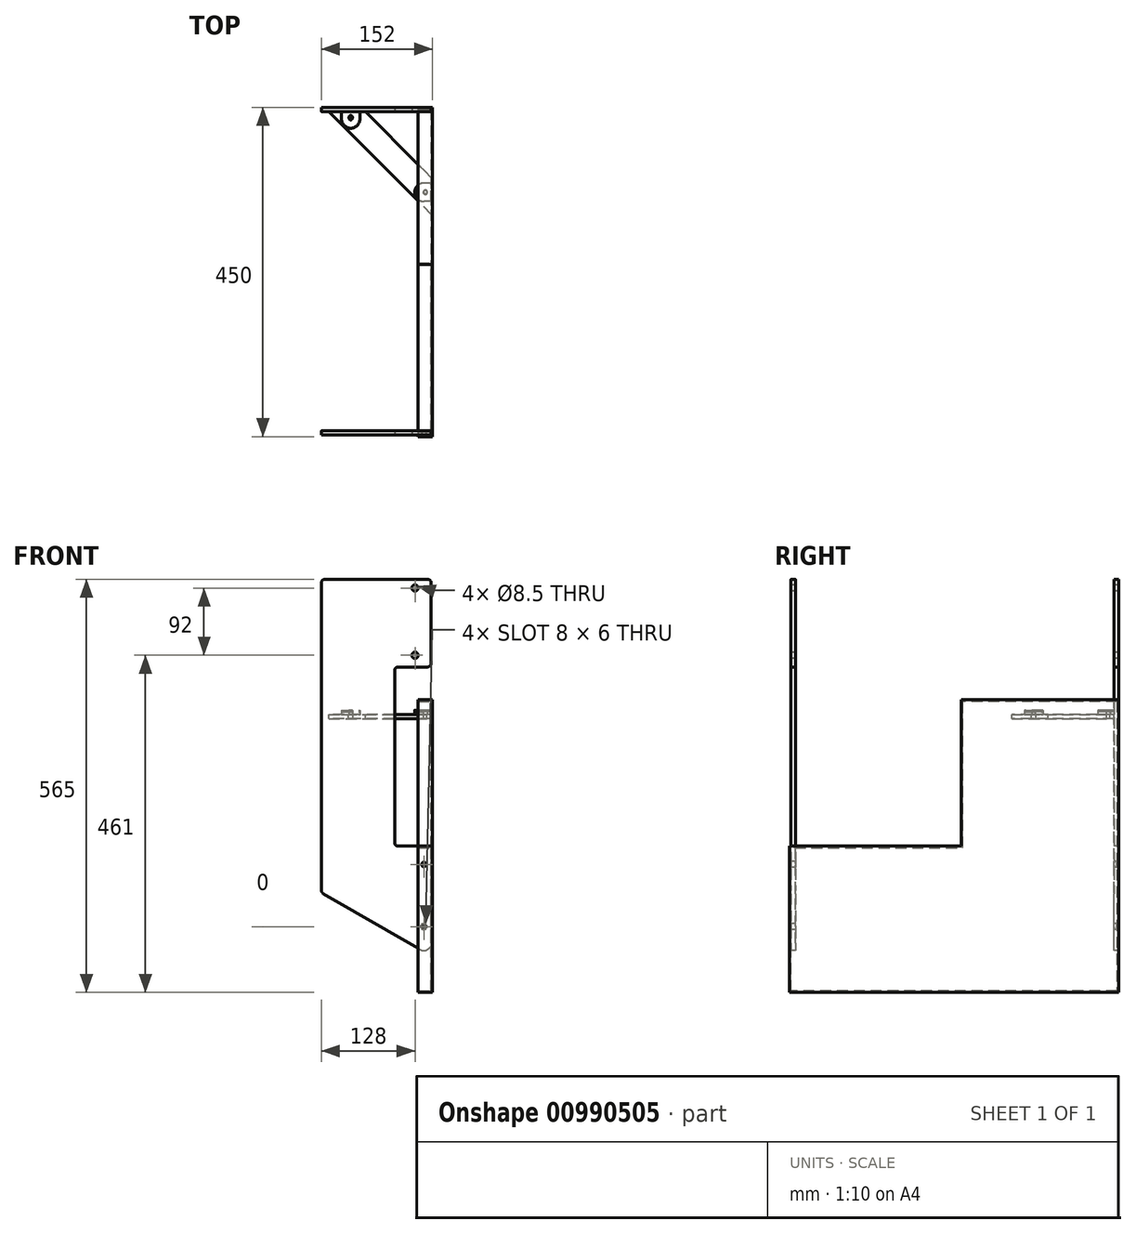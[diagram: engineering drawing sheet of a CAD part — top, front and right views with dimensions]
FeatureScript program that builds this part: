
annotation { "Feature Type Name" : "Feature", "Feature Type Description" : "" }
export const myFeature = defineFeature(function(context is Context, id is Id, definition is map)
    precondition{}
    {
        {
            var Q0;
            Q0=qCreatedBy(makeId("Right.planeOp"),FACE);
            var sketch = newSketch(context, id + "F0", { "sketchPlane" : qUnion([Q0])});
            skLineSegment(sketch, "E0", {"start": v(0, 0) * mm, "end": v(0, -400) * mm, "construction": true});
            skLineSegment(sketch, "E1", {"start": v(0, -200) * mm, "end": v(235, -200) * mm});
            skLineSegment(sketch, "E2", {"start": v(235, -200) * mm, "end": v(235, 0) * mm});
            skLineSegment(sketch, "E3", {"start": v(0, -400) * mm, "end": v(450, -400) * mm});
            skLineSegment(sketch, "E4", {"start": v(450, -400) * mm, "end": v(450, 0) * mm});
            skLineSegment(sketch, "E5", {"start": v(450, 0) * mm, "end": v(235, 0) * mm});
            skLineSegment(sketch, "E6", {"start": v(0, -200) * mm, "end": v(0, -400) * mm});
            skSolve(sketch);
        }
        {
            var Q0;
            Q0 = qSketchRegion(id + "F0", true);
            extrude(context, id + "F1", {"entities" : qUnion([Q0]), "depth" : 2 * mm, "offsetDistance" : 25 * mm});
        }
        {
            var Q0;
            Q0=makeQuery(id+"F1.opExtrude","CAP_FACE",FACE,{"disambiguationData":[OSD([sQuery(id+"F0.wireOp",EDGE,"E1"),sQuery(id+"F0.wireOp",EDGE,"E2"),sQuery(id+"F0.wireOp",EDGE,"E3"),sQuery(id+"F0.wireOp",EDGE,"E4"),sQuery(id+"F0.wireOp",EDGE,"E5"),sQuery(id+"F0.wireOp",EDGE,"E6")])],"isStart":false});
            var sketch = newSketch(context, id + "F2", { "sketchPlane" : qUnion([Q0])});
            skLineSegment(sketch, "E7", {"start": v(0, -200) * mm, "end": v(0, -400) * mm});
            skLineSegment(sketch, "E8", {"start": v(0, -400) * mm, "end": v(450, -400) * mm});
            skLineSegment(sketch, "E9", {"start": v(450, -400) * mm, "end": v(450, 0) * mm});
            skLineSegment(sketch, "E10", {"start": v(448, -2) * mm, "end": v(448, -398) * mm});
            skLineSegment(sketch, "E11", {"start": v(448, -398) * mm, "end": v(2, -398) * mm});
            skLineSegment(sketch, "E12", {"start": v(2, -398) * mm, "end": v(2, -200) * mm});
            skLineSegment(sketch, "E13.0", {"start": v(448, -2) * mm, "end": v(237, -2) * mm});
            skLineSegment(sketch, "E14.0", {"start": v(237, -202) * mm, "end": v(237, -2) * mm});
            skLineSegment(sketch, "E15.0", {"start": v(7, -202) * mm, "end": v(237, -202) * mm});
            skLineSegment(sketch, "E16", {"start": v(450, 0) * mm, "end": v(235, 0) * mm});
            skLineSegment(sketch, "E17", {"start": v(235, 0) * mm, "end": v(235, -200) * mm});
            skLineSegment(sketch, "E18", {"start": v(235, -200) * mm, "end": v(7, -200) * mm});
            skLineSegment(sketch, "E19", {"start": v(7, -202) * mm, "end": v(7, -200) * mm});
            skLineSegment(sketch, "E20.trimOffspring", {"start": v(2, -200) * mm, "end": v(0, -200) * mm});
            skSolve(sketch);
        }
        {
            var Q0;
            Q0 = qSketchRegion(id + "F2", true);
            extrude(context, id + "F3", {"entities" : qUnion([Q0]), "operationType" : NewBodyOperationType.ADD, "oppositeDirection" : true, "depth" : 20 * mm, "offsetDistance" : 25 * mm});
        }
        {
            var Q0;
            Q0=makeQuery(id+"F1.opExtrude","SWEPT_BODY",BODY,{"disambiguationData":[OSD([sQuery(id+"F0.wireOp",EDGE,"E1"),sQuery(id+"F0.wireOp",EDGE,"E2"),sQuery(id+"F0.wireOp",EDGE,"E3"),sQuery(id+"F0.wireOp",EDGE,"E4"),sQuery(id+"F0.wireOp",EDGE,"E5"),sQuery(id+"F0.wireOp",EDGE,"E6")])]});
            transform(context, id + "F4", {"entities" : qUnion([Q0]), "transformType" : TransformType.TRANSLATION_3D, "dx" : 0 * mm, "dy" : 0 * mm, "dz" : 0 * mm, "makeCopy" : true});
        }
        {
            var Q0;
            Q0=makeQuery(id+"F3.opExtrude","SWEPT_FACE",FACE,{"disambiguationData":[OSD([sQuery(id+"F2.wireOp",EDGE,"E10")])]});
            cPlane(context, id + "F5", {"entities" : qUnion([Q0]), "cplaneType" : CPlaneType.OFFSET, "offset" : 4 * mm, "width" : 150 * mm, "height" : 150 * mm});
        }
        {
            var Q0;
            Q0=qCreatedBy(id+"F5.planeOp",FACE);
            var sketch = newSketch(context, id + "F6", { "sketchPlane" : qUnion([Q0])});
            skLineSegment(sketch, "E21", {"start": v(-15, -341.34) * mm, "end": v(-147.5, -264.84) * mm});
            skLineSegment(sketch, "E22", {"start": v(0, -332.68) * mm, "end": v(0, -200) * mm});
            skLineSegment(sketch, "E23", {"start": v(0, -200) * mm, "end": v(-45, -200) * mm});
            skLineSegment(sketch, "E24", {"start": v(-50, -195) * mm, "end": v(-50, 40) * mm});
            skLineSegment(sketch, "E25", {"start": v(-45, 45) * mm, "end": v(-5, 45) * mm});
            skLineSegment(sketch, "E26", {"start": v(0, 50) * mm, "end": v(0, 160) * mm});
            skLineSegment(sketch, "E27", {"start": v(-5, 165) * mm, "end": v(-145, 165) * mm});
            skLineSegment(sketch, "E28", {"start": v(-150, 160) * mm, "end": v(-150, -260.51) * mm});
            skArc(sketch, "E29", {"start": v(0, 160) * mm, "mid": v(-1.46, 163.54) * mm, "end": v(-5, 165) * mm});
            skArc(sketch, "E30", {"start": v(-145, 165) * mm, "mid": v(-148.54, 163.54) * mm, "end": v(-150, 160) * mm});
            skArc(sketch, "E31", {"start": v(-150, -260.51) * mm, "mid": v(-149.33, -263.01) * mm, "end": v(-147.5, -264.84) * mm});
            skArc(sketch, "E32", {"start": v(-15, -341.34) * mm, "mid": v(-5, -341.34) * mm, "end": v(0, -332.68) * mm});
            skArc(sketch, "E33", {"start": v(-50, -195) * mm, "mid": v(-48.54, -198.54) * mm, "end": v(-45, -200) * mm});
            skArc(sketch, "E34", {"start": v(-45, 45) * mm, "mid": v(-48.54, 43.54) * mm, "end": v(-50, 40) * mm});
            skArc(sketch, "E35", {"start": v(-5, 45) * mm, "mid": v(-1.46, 46.46) * mm, "end": v(0, 50) * mm});
            skCircle(sketch, "E36", {"center": v(-22, 153) * mm, "radius": 4.25 * mm});
            skCircle(sketch, "E37", {"center": v(-22, 61) * mm, "radius": 4.25 * mm});
            skArc(sketch, "E38", {"start": v(-7, -224) * mm, "mid": v(-10, -221) * mm, "end": v(-13, -224) * mm});
            skArc(sketch, "E39", {"start": v(-13, -226) * mm, "mid": v(-10, -229) * mm, "end": v(-7, -226) * mm});
            skLineSegment(sketch, "E40", {"start": v(-7, -226) * mm, "end": v(-7, -224) * mm});
            skLineSegment(sketch, "E41", {"start": v(-13, -226) * mm, "end": v(-13, -224) * mm});
            skArc(sketch, "E42", {"start": v(-13, -311) * mm, "mid": v(-10, -314) * mm, "end": v(-7, -311) * mm});
            skArc(sketch, "E43", {"start": v(-7, -309) * mm, "mid": v(-10, -306) * mm, "end": v(-13, -309) * mm});
            skLineSegment(sketch, "E44", {"start": v(-7, -311) * mm, "end": v(-7, -309) * mm});
            skLineSegment(sketch, "E45", {"start": v(-13, -311) * mm, "end": v(-13, -309) * mm});
            skLineSegment(sketch, "E46", {"start": v(0, -200) * mm, "end": v(0, -350) * mm, "construction": true});
            skLineSegment(sketch, "E47", {"start": v(-147.5, -264.84) * mm, "end": v(0, -350) * mm, "construction": true});
            skLineSegment(sketch, "E48", {"start": v(-7, -225) * mm, "end": v(-13, -225) * mm, "construction": true});
            skLineSegment(sketch, "E49", {"start": v(-7, -310) * mm, "end": v(-13, -310) * mm, "construction": true});
            skLineSegment(sketch, "E50", {"start": v(-10, -224) * mm, "end": v(-10, -311) * mm, "construction": true});
            skSolve(sketch);
        }
        {
            var Q0;
            Q0 = qSketchRegion(id + "F6", true);
            extrude(context, id + "F7", {"entities" : qUnion([Q0]), "oppositeDirection" : true, "depth" : 6 * mm, "offsetDistance" : 25 * mm});
        }
        {
            var Q0;
            Q0=makeQuery(id+"F3.boolean.opBoolean","MERGE",FACE,{"derivedFrom":[makeQuery(id+"F1.opExtrude","SWEPT_FACE",FACE,{"disambiguationData":[OSD([sQuery(id+"F0.wireOp",EDGE,"E5")])]}),makeQuery(id+"F3.opExtrude","SWEPT_FACE",FACE,{"disambiguationData":[OSD([sQuery(id+"F2.wireOp",EDGE,"FrrXPd3z-IcxJ-MeG2-WEMV-cc5EvGv24Qu5")])]})]});
            cPlane(context, id + "F8", {"entities" : qUnion([Q0]), "cplaneType" : CPlaneType.OFFSET, "offset" : 20 * mm, "oppositeDirection" : true, "width" : 150 * mm, "height" : 150 * mm});
        }
        {
            var Q0;
            Q0=qCreatedBy(id+"F8.planeOp",FACE);
            var sketch = newSketch(context, id + "F9", { "sketchPlane" : qUnion([Q0])});
            skLineSegment(sketch, "E51", {"start": v(-122.5, 444) * mm, "end": v(-97.5, 444) * mm});
            skLineSegment(sketch, "E52", {"start": v(-110, 421.5) * mm, "end": v(-110, 444) * mm, "construction": true});
            skLineSegment(sketch, "E53", {"start": v(-122.5, 444) * mm, "end": v(-122.5, 434) * mm});
            skLineSegment(sketch, "E54", {"start": v(-97.5, 444) * mm, "end": v(-97.5, 434) * mm});
            skArc(sketch, "E55", {"start": v(-122.5, 434) * mm, "mid": v(-110, 421.5) * mm, "end": v(-97.5, 434) * mm});
            skArc(sketch, "E56", {"start": v(-107.75, 436.75) * mm, "mid": v(-110, 439) * mm, "end": v(-112.25, 436.75) * mm});
            skArc(sketch, "E57.MirrorC", {"start": v(-107.75, 435.25) * mm, "mid": v(-110, 433) * mm, "end": v(-112.25, 435.25) * mm});
            skLineSegment(sketch, "E58", {"start": v(-112.25, 436.75) * mm, "end": v(-112.25, 435.25) * mm});
            skLineSegment(sketch, "E59", {"start": v(-107.75, 436.75) * mm, "end": v(-107.75, 435.25) * mm});
            skLineSegment(sketch, "E60", {"start": v(-112.25, 436) * mm, "end": v(-107.75, 436) * mm, "construction": true});
            skLineSegment(sketch, "E61", {"start": v(-20, 424) * mm, "end": v(0, 444) * mm, "construction": true});
            skLineSegment(sketch, "E62.MirrorCS", {"start": v(-8, 331.75) * mm, "end": v(-8, 336.25) * mm, "construction": true});
            skArc(sketch, "E63.MirrorCS", {"start": v(-7.25, 336.25) * mm, "mid": v(-5, 334) * mm, "end": v(-7.25, 331.75) * mm});
            skLineSegment(sketch, "E64.MirrorCS", {"start": v(-7.25, 336.25) * mm, "end": v(-8.75, 336.25) * mm});
            skLineSegment(sketch, "E65.MirrorCS", {"start": v(-7.25, 331.75) * mm, "end": v(-8.75, 331.75) * mm});
            skArc(sketch, "E66.MirrorCS", {"start": v(-8.75, 336.25) * mm, "mid": v(-11, 334) * mm, "end": v(-8.75, 331.75) * mm});
            skLineSegment(sketch, "E67.MirrorCS", {"start": v(0, 321.5) * mm, "end": v(0, 346.5) * mm});
            skLineSegment(sketch, "E68.MirrorCS", {"start": v(0, 321.5) * mm, "end": v(-10, 321.5) * mm});
            skArc(sketch, "E69.MirrorCS", {"start": v(-10, 321.5) * mm, "mid": v(-22.5, 334) * mm, "end": v(-10, 346.5) * mm});
            skLineSegment(sketch, "E70.MirrorCS", {"start": v(-22.5, 334) * mm, "end": v(0, 334) * mm, "construction": true});
            skLineSegment(sketch, "E71.MirrorCS", {"start": v(0, 346.5) * mm, "end": v(-10, 346.5) * mm});
            skSolve(sketch);
        }
        {
            var Q0;
            Q0=makeQuery(id+"F9.imprint","IMPRINT",FACE,{"disambiguationData":[TD([[makeQuery(id+"F9.imprint","IMPRINT",EDGE,{"derivedFrom":sQuery(id+"F9.wireOp",EDGE,"E51")}),-1.0]])]});
            extrude(context, id + "F10", {"entities" : qUnion([Q0]), "depth" : 4 * mm, "offsetDistance" : 25 * mm});
        }
        {
            var Q0;
            Q0 = qSketchRegion(id + "F9", true);
            extrude(context, id + "F11", {"entities" : qUnion([Q0]), "depth" : 6 * mm, "offsetDistance" : 25 * mm});
        }
        {
            var Q0;
            Q0=makeQuery(id+"F3.boolean.opBoolean","MERGE",FACE,{"derivedFrom":[makeQuery(id+"F1.opExtrude","SWEPT_FACE",FACE,{"disambiguationData":[OSD([sQuery(id+"F0.wireOp",EDGE,"E4")])]}),makeQuery(id+"F3.opExtrude","SWEPT_FACE",FACE,{"disambiguationData":[OSD([sQuery(id+"F2.wireOp",EDGE,"E9")])]})]});
            var sketch = newSketch(context, id + "F12", { "sketchPlane" : qUnion([Q0])});
            skCircle(sketch, "E72", {"center": v(10, -310) * mm, "radius": 3 * mm});
            skCircle(sketch, "E73", {"center": v(10, -225) * mm, "radius": 3 * mm});
            skLineSegment(sketch, "E74", {"start": v(7, -225) * mm, "end": v(13, -225) * mm, "construction": true});
            skLineSegment(sketch, "E75", {"start": v(10, -221) * mm, "end": v(10, -229) * mm, "construction": true});
            skLineSegment(sketch, "E76", {"start": v(7, -310) * mm, "end": v(13, -310) * mm, "construction": true});
            skLineSegment(sketch, "E77", {"start": v(10, -306) * mm, "end": v(10, -314) * mm, "construction": true});
            skSolve(sketch);
        }
        {
            var Q0;
            Q0 = qSketchRegion(id + "F12", true);
            var Q1;
            Q1=makeQuery(id+"F3.boolean.opBoolean","MERGE",FACE,{"derivedFrom":[makeQuery(id+"F1.opExtrude","SWEPT_FACE",FACE,{"disambiguationData":[OSD([sQuery(id+"F0.wireOp",EDGE,"E6")])]}),makeQuery(id+"F3.opExtrude","SWEPT_FACE",FACE,{"disambiguationData":[OSD([sQuery(id+"F2.wireOp",EDGE,"E7")])]})]});
            extrude(context, id + "F13", {"entities" : qUnion([Q0]), "endBound" : BoundingType.UP_TO_SURFACE, "oppositeDirection" : true, "depth" : 25 * mm, "endBoundEntityFace" : qUnion([Q1]), "offsetDistance" : 25 * mm});
        }
        {
            var Q0;
            Q0=makeQuery(id+"F13.opExtrude","SWEPT_BODY",BODY,{"disambiguationData":[OSD([sQuery(id+"F12.wireOp",EDGE,"E72")])]});
            var Q1;
            Q1=makeQuery(id+"F13.opExtrude","SWEPT_BODY",BODY,{"disambiguationData":[OSD([sQuery(id+"F12.wireOp",EDGE,"E73")])]});
            var Q2;
            Q2=makeQuery(id+"F1.opExtrude","SWEPT_BODY",BODY,{"disambiguationData":[OSD([sQuery(id+"F0.wireOp",EDGE,"E1"),sQuery(id+"F0.wireOp",EDGE,"E2"),sQuery(id+"F0.wireOp",EDGE,"E3"),sQuery(id+"F0.wireOp",EDGE,"E4"),sQuery(id+"F0.wireOp",EDGE,"E5"),sQuery(id+"F0.wireOp",EDGE,"E6")])]});
            booleanBodies(context, id + "F14", {"operationType" : BooleanOperationType.SUBTRACTION, "tools" : qUnion([Q0, Q1]), "targets" : qUnion([Q2])});
        }
        {
            var Q0;
            Q0=makeQuery(id+"F11.opExtrude","SWEPT_BODY",BODY,{"disambiguationData":[OSD([sQuery(id+"F9.wireOp",EDGE,"E63.MirrorCS"),sQuery(id+"F9.wireOp",EDGE,"E64.MirrorCS"),sQuery(id+"F9.wireOp",EDGE,"E65.MirrorCS"),sQuery(id+"F9.wireOp",EDGE,"E66.MirrorCS"),sQuery(id+"F9.wireOp",EDGE,"E67.MirrorCS"),sQuery(id+"F9.wireOp",EDGE,"E68.MirrorCS"),sQuery(id+"F9.wireOp",EDGE,"E69.MirrorCS"),sQuery(id+"F9.wireOp",EDGE,"E71.MirrorCS")])]});
            transform(context, id + "F15", {"entities" : qUnion([Q0]), "transformType" : TransformType.TRANSLATION_3D, "dx" : 0 * mm, "dy" : 0 * mm, "dz" : 0 * mm, "makeCopy" : true});
        }
        {
            var Q0;
            Q0=qCreatedBy(makeId("Front.planeOp"),FACE);
            cPlane(context, id + "F16", {"entities" : qUnion([Q0]), "cplaneType" : CPlaneType.OFFSET, "offset" : 2 * mm, "oppositeDirection" : true, "width" : 150 * mm, "height" : 150 * mm});
        }
        {
            var Q0;
            Q0=makeQuery(id+"F3.opExtrude","SWEPT_FACE",FACE,{"disambiguationData":[OSD([sQuery(id+"F2.wireOp",EDGE,"E12")])]});
            var Q1;
            Q1=makeQuery(id+"F3.opExtrude","SWEPT_FACE",FACE,{"disambiguationData":[OSD([sQuery(id+"F2.wireOp",EDGE,"E12")])]});
            var Q2;
            Q2=makeQuery(id+"F3.opExtrude","SWEPT_FACE",FACE,{"disambiguationData":[OSD([sQuery(id+"F2.wireOp",EDGE,"E12")])]});
            var Q3;
            Q3=qCreatedBy(id+"F16.planeOp",FACE);
            var Q4;
            Q4=makeQuery(id+"F3.opExtrude","SWEPT_FACE",FACE,{"disambiguationData":[OSD([sQuery(id+"F2.wireOp",EDGE,"E12")])]});
            var Q5;
            Q5=qCreatedBy(id+"F16.planeOp",FACE);
            var Q6;
            Q6=makeQuery(id+"F3.boolean.opBoolean","MERGE",FACE,{"derivedFrom":[makeQuery(id+"F1.opExtrude","SWEPT_FACE",FACE,{"disambiguationData":[OSD([sQuery(id+"F0.wireOp",EDGE,"E6")])]}),makeQuery(id+"F3.opExtrude","SWEPT_FACE",FACE,{"disambiguationData":[OSD([sQuery(id+"F2.wireOp",EDGE,"E7")])]})]});
            var Q7;
            Q7=qCreatedBy(id+"F16.planeOp",FACE);
            var sketch = newSketch(context, id + "F17", { "sketchPlane" : qUnion([Q0, Q1, Q2, Q3, Q4, Q5, Q6, Q7])});
            skLineSegment(sketch, "E78", {"start": v(5, 165) * mm, "end": v(145, 165) * mm});
            skLineSegment(sketch, "E79", {"start": v(150, 160) * mm, "end": v(150, -260.51) * mm});
            skLineSegment(sketch, "E80", {"start": v(147.5, -264.84) * mm, "end": v(15, -341.34) * mm});
            skLineSegment(sketch, "E81", {"start": v(0, -332.68) * mm, "end": v(0, -200) * mm});
            skLineSegment(sketch, "E82", {"start": v(0, -200) * mm, "end": v(45, -200) * mm});
            skLineSegment(sketch, "E83", {"start": v(45, 45) * mm, "end": v(5, 45) * mm});
            skLineSegment(sketch, "E84", {"start": v(0, 50) * mm, "end": v(0, 160) * mm});
            skLineSegment(sketch, "E85", {"start": v(50, -195) * mm, "end": v(50, 40) * mm});
            skArc(sketch, "E86", {"start": v(0, -332.68) * mm, "mid": v(5, -341.34) * mm, "end": v(15, -341.34) * mm});
            skArc(sketch, "E87", {"start": v(147.5, -264.84) * mm, "mid": v(149.33, -263.01) * mm, "end": v(150, -260.51) * mm});
            skArc(sketch, "E88", {"start": v(150, 160) * mm, "mid": v(148.54, 163.54) * mm, "end": v(145, 165) * mm});
            skArc(sketch, "E89", {"start": v(5, 165) * mm, "mid": v(1.46, 163.54) * mm, "end": v(0, 160) * mm});
            skArc(sketch, "E90", {"start": v(0, 50) * mm, "mid": v(1.46, 46.46) * mm, "end": v(5, 45) * mm});
            skArc(sketch, "E91", {"start": v(50, 40) * mm, "mid": v(48.54, 43.54) * mm, "end": v(45, 45) * mm});
            skArc(sketch, "E92", {"start": v(45, -200) * mm, "mid": v(48.54, -198.54) * mm, "end": v(50, -195) * mm});
            skCircle(sketch, "E93", {"center": v(22, 153) * mm, "radius": 4.25 * mm});
            skCircle(sketch, "E94", {"center": v(22, 61) * mm, "radius": 4.25 * mm});
            skArc(sketch, "E95", {"start": v(13, -224) * mm, "mid": v(10, -221) * mm, "end": v(7, -224) * mm});
            skArc(sketch, "E96", {"start": v(7, -226) * mm, "mid": v(10, -229) * mm, "end": v(13, -226) * mm});
            skLineSegment(sketch, "E97", {"start": v(7, -224) * mm, "end": v(7, -226) * mm});
            skLineSegment(sketch, "E98", {"start": v(13, -224) * mm, "end": v(13, -226) * mm});
            skArc(sketch, "E99", {"start": v(13, -309) * mm, "mid": v(10, -306) * mm, "end": v(7, -309) * mm});
            skArc(sketch, "E100", {"start": v(7, -311) * mm, "mid": v(10, -314) * mm, "end": v(13, -311) * mm});
            skLineSegment(sketch, "E101", {"start": v(7, -309) * mm, "end": v(7, -311) * mm});
            skLineSegment(sketch, "E102", {"start": v(13, -309) * mm, "end": v(13, -311) * mm});
            skSolve(sketch);
        }
        {
            var Q0;
            Q0 = qSketchRegion(id + "F17", true);
            extrude(context, id + "F18", {"entities" : qUnion([Q0]), "depth" : 6 * mm, "offsetDistance" : 25 * mm});
        }
        {
            var Q0;
            Q0=qCreatedBy(makeId("Top.planeOp"),FACE);
            cPlane(context, id + "F19", {"entities" : qUnion([Q0]), "cplaneType" : CPlaneType.OFFSET, "offset" : 20 * mm, "oppositeDirection" : true, "width" : 150 * mm, "height" : 150 * mm});
        }
        {
            var Q0;
            Q0=qCreatedBy(id+"F19.planeOp",FACE);
            var sketch = newSketch(context, id + "F20", { "sketchPlane" : qUnion([Q0])});
            skLineSegment(sketch, "E103", {"start": v(0, 321.5) * mm, "end": v(0, 346.5) * mm});
            skLineSegment(sketch, "E104", {"start": v(0, 321.5) * mm, "end": v(-10, 321.5) * mm});
            skLineSegment(sketch, "E105", {"start": v(0, 346.5) * mm, "end": v(-10, 346.5) * mm});
            skArc(sketch, "E106", {"start": v(-10, 346.5) * mm, "mid": v(-22.5, 334) * mm, "end": v(-10, 321.5) * mm});
            skSolve(sketch);
        }
        {
            var Q0;
            Q0 = qSketchRegion(id + "F20", true);
            extrude(context, id + "F21", {"entities" : qUnion([Q0]), "depth" : 4 * mm, "offsetDistance" : 25 * mm});
        }
        {
            var Q0;
            Q0=qCreatedBy(id+"F19.planeOp",FACE);
            var sketch = newSketch(context, id + "F22", { "sketchPlane" : qUnion([Q0])});
            skLineSegment(sketch, "E107", {"start": v(0, 304) * mm, "end": v(-140, 444) * mm});
            skLineSegment(sketch, "E108", {"start": v(-140, 444) * mm, "end": v(-90, 444) * mm});
            skLineSegment(sketch, "E109", {"start": v(-90, 444) * mm, "end": v(0, 354) * mm});
            skLineSegment(sketch, "E110", {"start": v(0, 354) * mm, "end": v(0, 304) * mm});
            skLineSegment(sketch, "E111", {"start": v(-10.1, 334.9) * mm, "end": v(-10.1, 333.1) * mm});
            skLineSegment(sketch, "E112", {"start": v(-5.9, 334.9) * mm, "end": v(-5.9, 333.1) * mm});
            skArc(sketch, "E113", {"start": v(-10.1, 333.1) * mm, "mid": v(-8, 331) * mm, "end": v(-5.9, 333.1) * mm});
            skArc(sketch, "E114", {"start": v(-5.9, 334.9) * mm, "mid": v(-8, 337) * mm, "end": v(-10.1, 334.9) * mm});
            skLineSegment(sketch, "E115", {"start": v(-8, 331) * mm, "end": v(-8, 337) * mm, "construction": true});
            skLineSegment(sketch, "E116", {"start": v(-10.1, 334) * mm, "end": v(-5.9, 334) * mm, "construction": true});
            skLineSegment(sketch, "E117", {"start": v(-8, 331.75) * mm, "end": v(-8, 336.25) * mm, "construction": true});
            skLineSegment(sketch, "E118", {"start": v(-11, 334) * mm, "end": v(-5, 334) * mm, "construction": true});
            skLineSegment(sketch, "E119", {"start": v(-20, 424) * mm, "end": v(0, 444) * mm, "construction": true});
            skLineSegment(sketch, "E120.MirrorCS", {"start": v(-109.1, 438.1) * mm, "end": v(-110.9, 438.1) * mm});
            skLineSegment(sketch, "E121.MirrorCS", {"start": v(-109.1, 433.9) * mm, "end": v(-110.9, 433.9) * mm});
            skLineSegment(sketch, "E122.MirrorCS", {"start": v(-112.25, 436) * mm, "end": v(-107.75, 436) * mm, "construction": true});
            skLineSegment(sketch, "E123.MirrorCS", {"start": v(-110, 433.9) * mm, "end": v(-110, 438.1) * mm, "construction": true});
            skLineSegment(sketch, "E124.MirrorCS", {"start": v(-110, 433) * mm, "end": v(-110, 439) * mm, "construction": true});
            skLineSegment(sketch, "E125.MirrorCS", {"start": v(-113, 436) * mm, "end": v(-107, 436) * mm, "construction": true});
            skArc(sketch, "E126.MirrorCS", {"start": v(-110.9, 433.9) * mm, "mid": v(-113, 436) * mm, "end": v(-110.9, 438.1) * mm});
            skArc(sketch, "E127.MirrorCS", {"start": v(-109.1, 438.1) * mm, "mid": v(-107, 436) * mm, "end": v(-109.1, 433.9) * mm});
            skSolve(sketch);
        }
        {
            var Q0;
            Q0 = qSketchRegion(id + "F22", true);
            extrude(context, id + "F23", {"entities" : qUnion([Q0]), "oppositeDirection" : true, "depth" : 6 * mm, "offsetDistance" : 25 * mm});
        }
    });
